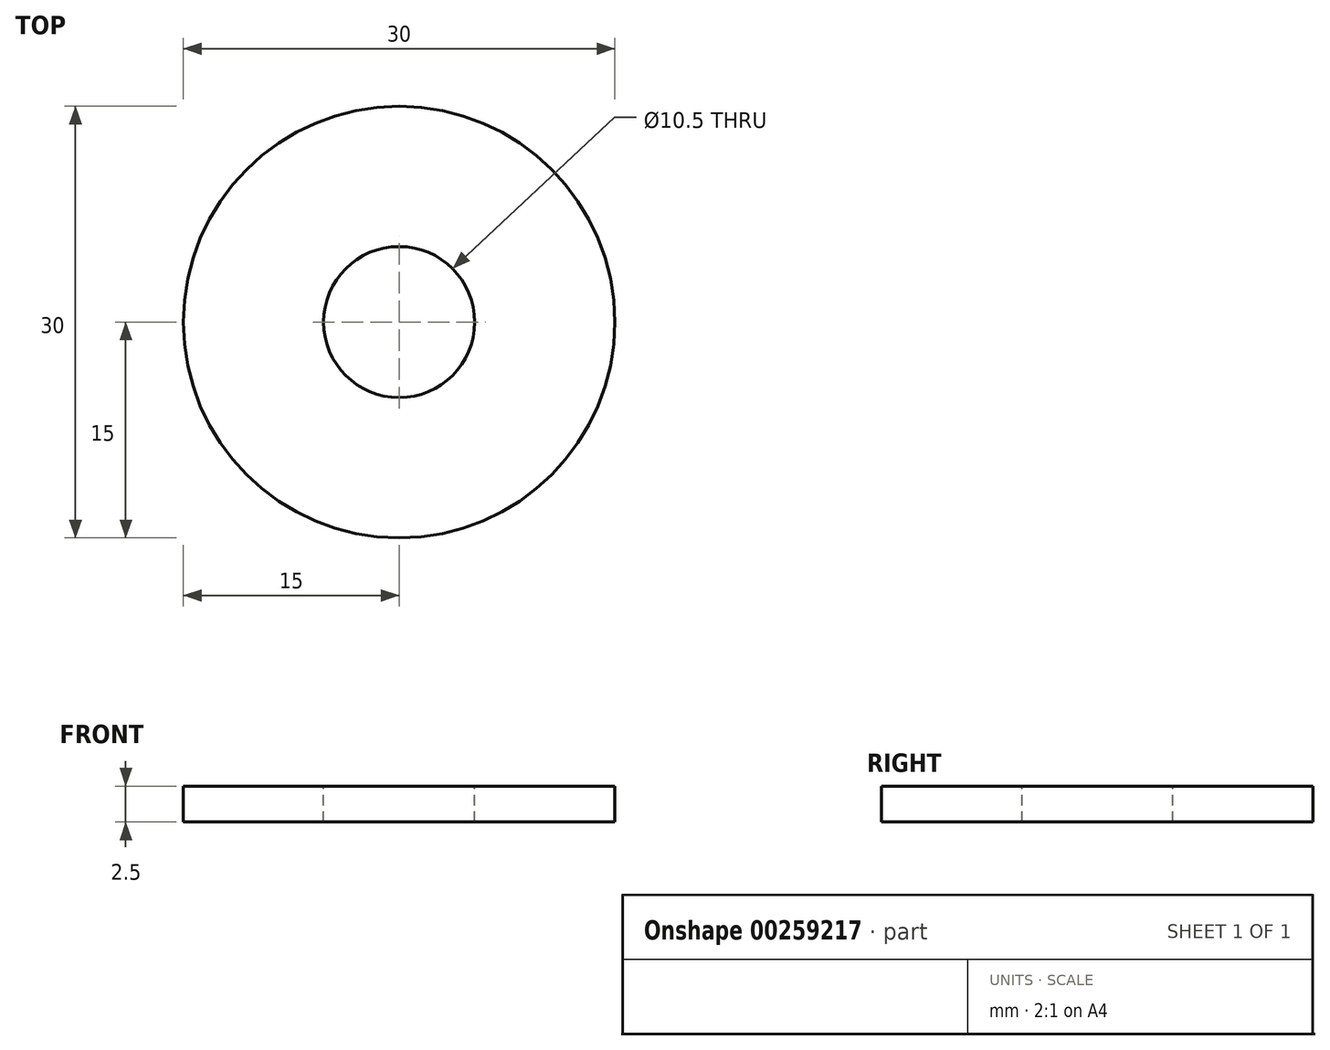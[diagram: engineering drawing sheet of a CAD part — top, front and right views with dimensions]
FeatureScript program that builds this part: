
annotation { "Feature Type Name" : "Feature", "Feature Type Description" : "" }
export const myFeature = defineFeature(function(context is Context, id is Id, definition is map)
    precondition{}
    {
        {
            var Q0;
            Q0=qCreatedBy(makeId("Front.planeOp"),FACE);
            var sketch = newSketch(context, id + "F0", { "sketchPlane" : qUnion([Q0])});
            skLineSegment(sketch, "E0", {"start": v(-15, 2.5) * mm, "end": v(-5.25, 2.5) * mm});
            skLineSegment(sketch, "E1", {"start": v(-5.25, 0) * mm, "end": v(-5.25, 2.5) * mm});
            skLineSegment(sketch, "E2", {"start": v(-15, 0) * mm, "end": v(-15, 2.5) * mm});
            skLineSegment(sketch, "E3", {"start": v(-15, 0) * mm, "end": v(-5.25, 0) * mm});
            skPoint(sketch, "E4.orphan", {"position": v(0, 2.5) * mm});
            skLineSegment(sketch, "E5", {"start": v(0, 25.32) * mm, "end": v(0, -10.45) * mm, "construction": true});
            skSolve(sketch);
        }
        {
            var Q0;
            Q0=qSketchRegion(id+"F0",true);
            var Q1;
            Q1=sQuery(id+"F0.wireOp",EDGE,"E5");
            revolve(context, id + "F1", {"entities" : qUnion([Q0]), "axis" : qUnion([Q1]), "revolveType" : RevolveType.FULL});
        }
    });
